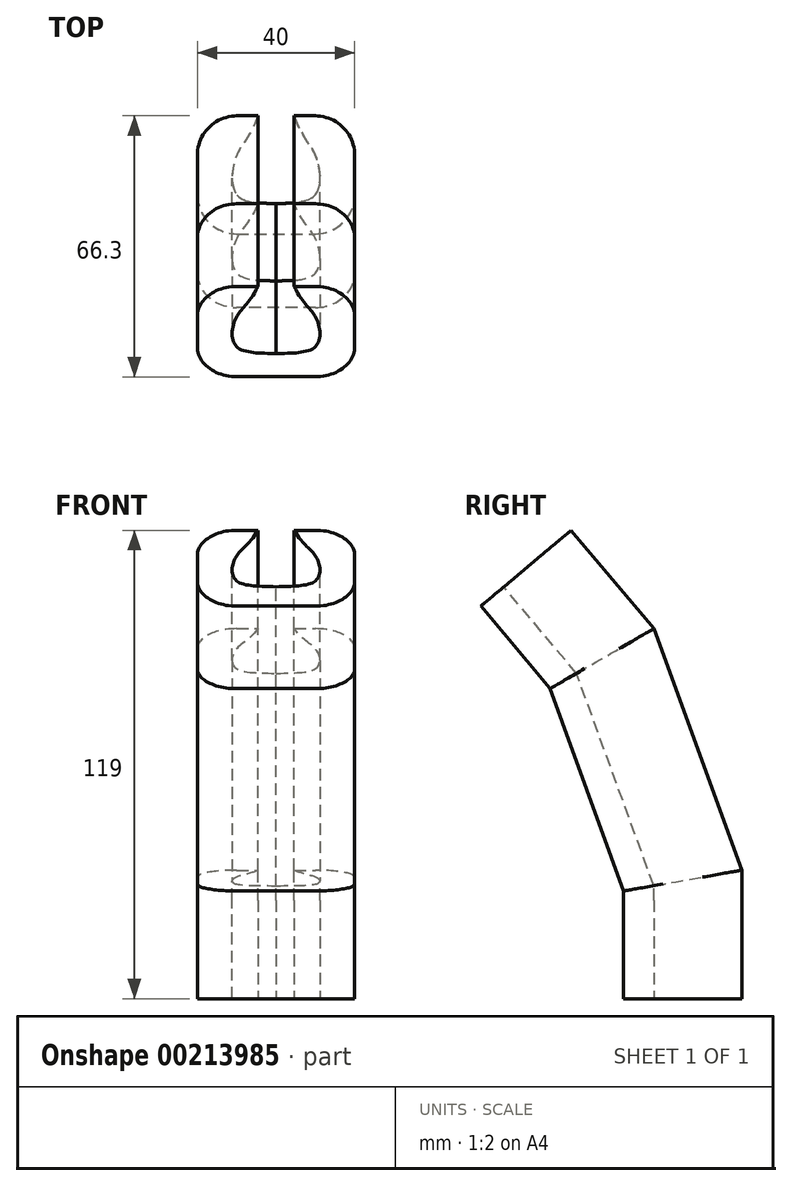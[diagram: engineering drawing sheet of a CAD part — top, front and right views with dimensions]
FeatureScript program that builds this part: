
annotation { "Feature Type Name" : "Feature", "Feature Type Description" : "" }
export const myFeature = defineFeature(function(context is Context, id is Id, definition is map)
    precondition{}
    {
        {
            var Q0;
            Q0=qCreatedBy(makeId("Top.planeOp"),FACE);
            var sketch = newSketch(context, id + "F0", { "sketchPlane" : qUnion([Q0])});
            skLineSegment(sketch, "E0.bottom", {"start": v(-10, 15) * mm, "end": v(-4.61, 15) * mm});
            skLineSegment(sketch, "E0.top", {"start": v(-10, -15) * mm, "end": v(10, -15) * mm});
            skLineSegment(sketch, "E0.left", {"start": v(-20, 5) * mm, "end": v(-20, -5) * mm});
            skLineSegment(sketch, "E0.right", {"start": v(20, 5) * mm, "end": v(20, -5) * mm});
            skPoint(sketch, "E0.middle", {"position": v(0, 0) * mm});
            skPoint(sketch, "E1.visualSharp", {"position": v(-20, 15) * mm});
            skArc(sketch, "E1.filletArc", {"start": v(-10, 15) * mm, "mid": v(-17.07, 12.07) * mm, "end": v(-20, 5) * mm});
            skPoint(sketch, "E2.visualSharp", {"position": v(20, 15) * mm});
            skArc(sketch, "E2.filletArc", {"start": v(20, 5) * mm, "mid": v(17.07, 12.07) * mm, "end": v(10, 15) * mm});
            skPoint(sketch, "E3.visualSharp", {"position": v(20, -15) * mm});
            skArc(sketch, "E3.filletArc", {"start": v(10, -15) * mm, "mid": v(17.07, -12.07) * mm, "end": v(20, -5) * mm});
            skPoint(sketch, "E4.visualSharp", {"position": v(-20, -15) * mm});
            skArc(sketch, "E4.filletArc", {"start": v(-20, -5) * mm, "mid": v(-17.07, -12.07) * mm, "end": v(-10, -15) * mm});
            skFitSpline(sketch, "E5", {"points": [v(-4.61, 15) * mm, v(-10, 5) * mm, v(-10, -5) * mm, v(0, -7.35) * mm], "startDerivative": vector(-19.21, -52.82) * mm, "endDerivative": vector(34.18, -2.24) * mm});
            skFitSpline(sketch, "E6.MirrorCS", {"points": [v(4.61, 15) * mm, v(10, 5) * mm, v(10, -5) * mm, v(0, -7.35) * mm], "startDerivative": vector(19.21, -52.82) * mm, "endDerivative": vector(-34.18, -2.24) * mm});
            skLineSegment(sketch, "E7.trimOffspring", {"start": v(4.61, 15) * mm, "end": v(10, 15) * mm});
            skSolve(sketch);
        }
        {
            var Q0;
            Q0=qCreatedBy(makeId("Right.planeOp"),FACE);
            var sketch = newSketch(context, id + "F1", { "sketchPlane" : qUnion([Q0])});
            skLineSegment(sketch, "E8", {"start": v(0, 0) * mm, "end": v(0, 30) * mm});
            skLineSegment(sketch, "E9", {"start": v(0, 30) * mm, "end": v(0, 105.74) * mm, "construction": true});
            skLineSegment(sketch, "E10.MirrorCS", {"start": v(0, 30) * mm, "end": v(-20.52, 86.38) * mm});
            skLineSegment(sketch, "E11.MirrorCS", {"start": v(-39.8, 109.36) * mm, "end": v(-20.52, 86.38) * mm});
            skSolve(sketch);
        }
        {
            var Q0;
            Q0 = qSketchRegion(id + "F0", true);
            extrude(context, id + "F2", {"entities" : qUnion([Q0]), "depth" : 25 * mm});
        }
        {
            var Q0;
            Q0 = qSketchRegion(id + "F0", true);
            var Q1;
            Q1 = qConstructionFilter(qBodyType(qCreatedBy(id + "F1" ,EDGE), BodyType.WIRE), ConstructionObject.NO);
            sweep(context, id + "F3", {"operationType" : NewBodyOperationType.ADD, "profiles" : qUnion([Q0]), "path" : qUnion([Q1])});
        }
    });
